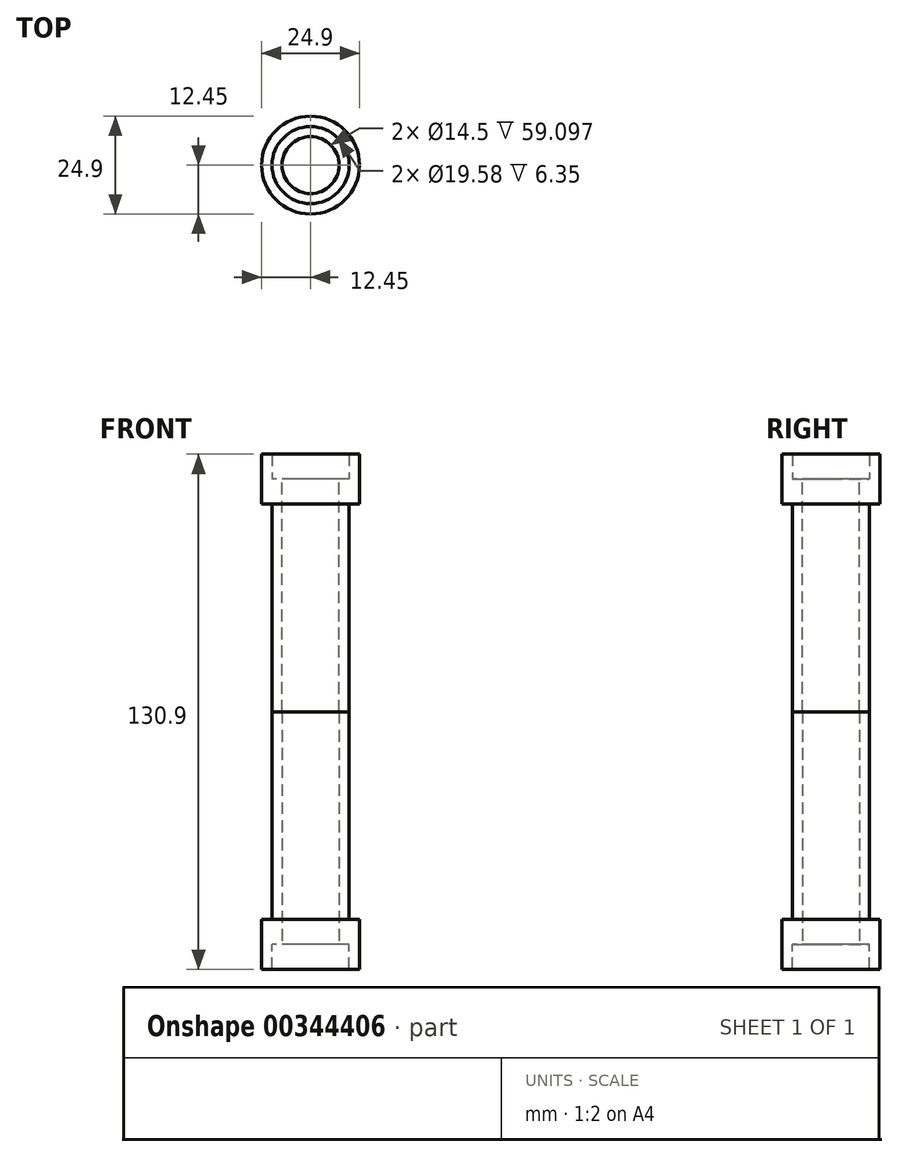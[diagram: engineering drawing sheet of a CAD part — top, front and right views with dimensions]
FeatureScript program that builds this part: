
annotation { "Feature Type Name" : "Feature", "Feature Type Description" : "" }
export const myFeature = defineFeature(function(context is Context, id is Id, definition is map)
    precondition{}
    {
        {
            var Q0;
            Q0=qCreatedBy(makeId("Top.planeOp"),FACE);
            var sketch = newSketch(context, id + "F0", { "sketchPlane" : qUnion([Q0])});
            skCircle(sketch, "E0", {"center": v(0, 0) * mm, "radius": 9.79 * mm});
            skSolve(sketch);
        }
        {
            var Q0;
            Q0=qCreatedBy(makeId("Front.planeOp"),FACE);
            var sketch = newSketch(context, id + "F1", { "sketchPlane" : qUnion([Q0])});
            skLineSegment(sketch, "E1", {"start": v(0, 0) * mm, "end": v(0, 59.1) * mm});
            skSolve(sketch);
        }
        {
            var Q0;
            Q0=makeQuery(id+"F0.imprint","IMPRINT",FACE,{"disambiguationData":[TD([[makeQuery(id+"F0.imprint","IMPRINT",EDGE,{"derivedFrom":sQuery(id+"F0.wireOp",EDGE,"E0")}),1.0]])]});
            var Q1;
            Q1=sQuery(id+"F1.wireOp",EDGE,"E1");
            sweep(context, id + "F2", {"profiles" : qUnion([Q0]), "path" : qUnion([Q1])});
        }
        {
            var Q0;
            Q0=makeQuery(id+"F2.opSweep","CAP_FACE",FACE,{"disambiguationData":[OSD([sQuery(id+"F0.wireOp",EDGE,"E0"),sQuery(id+"F1.wireOp",VERTEX,"E1.end")])],"isStart":false});
            var Q1;
            Q1=makeQuery(id+"F2.opSweep","CAP_FACE",FACE,{"disambiguationData":[OSD([sQuery(id+"F0.wireOp",EDGE,"E0"),sQuery(id+"F1.wireOp",VERTEX,"E1.start")])],"isStart":true});
            shell(context, id + "F3", {"entities" : qUnion([Q0, Q1]), "thickness" : 2.54 * mm});
        }
        {
            var Q0;
            Q0=makeQuery(id+"F2.opSweep","CAP_FACE",FACE,{"disambiguationData":[OSD([sQuery(id+"F0.wireOp",EDGE,"E0"),sQuery(id+"F1.wireOp",VERTEX,"E1.end")])],"isStart":false});
            var sketch = newSketch(context, id + "F4", { "sketchPlane" : qUnion([Q0])});
            skCircle(sketch, "E2", {"center": v(0, 0) * mm, "radius": 12.45 * mm});
            skSolve(sketch);
        }
        {
            var Q0;
            Q0=makeQuery(id+"F4.imprint","IMPRINT",FACE,{"disambiguationData":[TD([[makeQuery(id+"F4.imprint","IMPRINT",EDGE,{"derivedFrom":sQuery(id+"F4.wireOp",EDGE,"E2")}),1.0]])]});
            extrude(context, id + "F5", {"entities" : qUnion([Q0]), "operationType" : NewBodyOperationType.ADD, "endBound" : BoundingType.SYMMETRIC, "depth" : 12.7 * mm});
        }
        {
            var Q0;
            Q0=makeQuery(id+"F2.opSweep","SWEPT_BODY",BODY,{"disambiguationData":[OSD([sQuery(id+"F0.wireOp",EDGE,"E0"),sQuery(id+"F1.wireOp",EDGE,"E1")])]});
            var Q1;
            Q1=qCreatedBy(makeId("Top.planeOp"),FACE);
            mirror(context, id + "F6", {"entities" : qUnion([Q0]), "mirrorPlane" : qUnion([Q1])});
        }
    });
